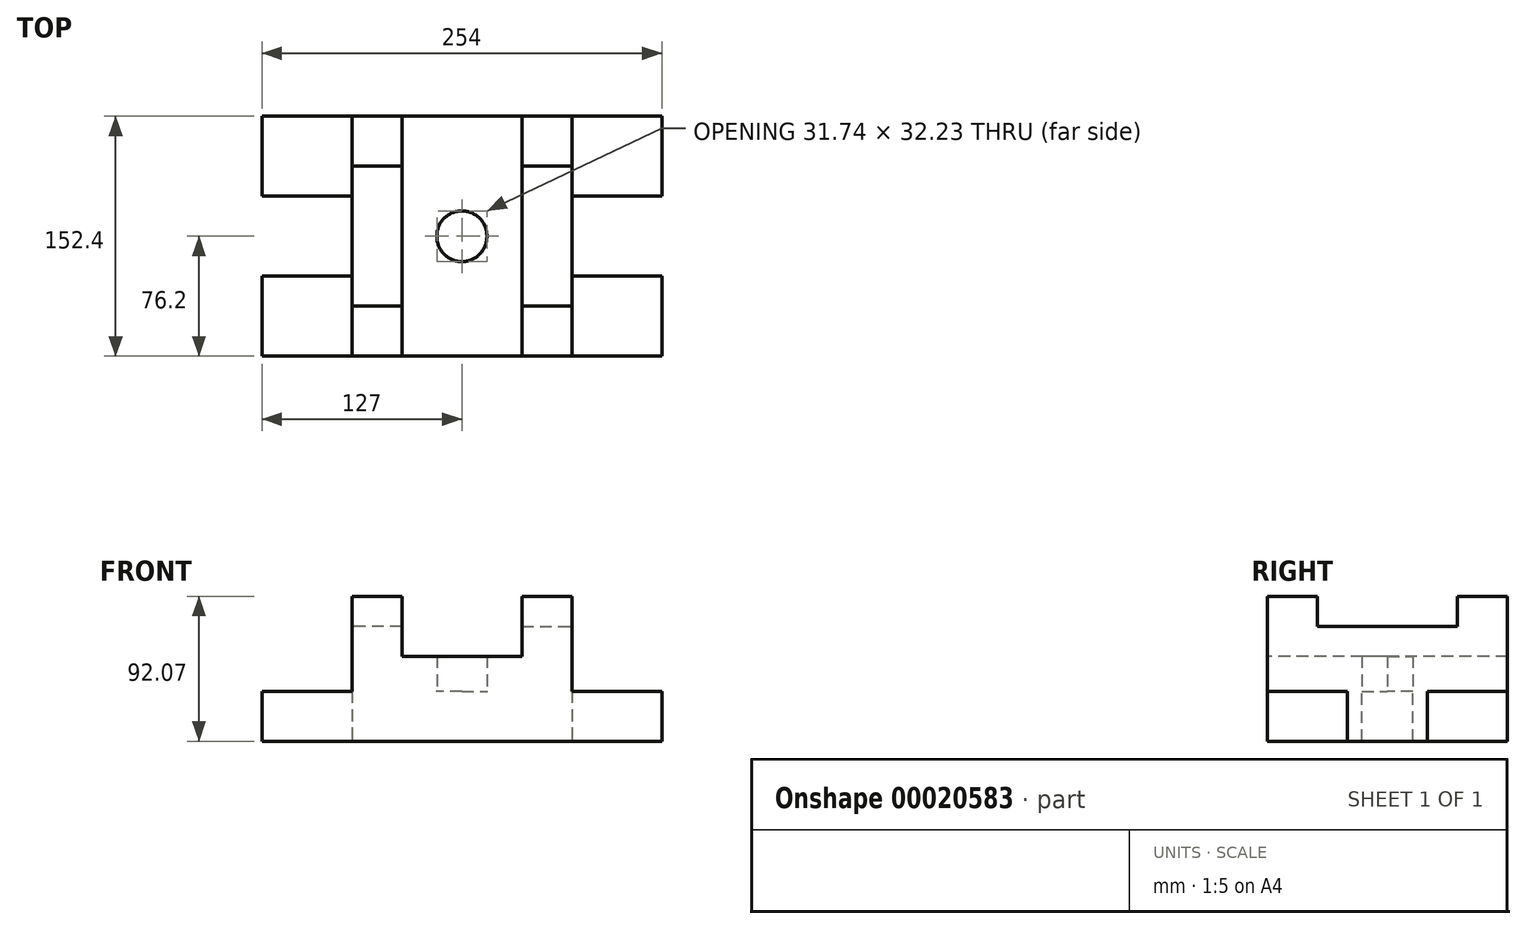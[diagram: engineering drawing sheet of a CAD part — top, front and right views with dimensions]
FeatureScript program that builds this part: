
annotation { "Feature Type Name" : "Feature", "Feature Type Description" : "" }
export const myFeature = defineFeature(function(context is Context, id is Id, definition is map)
    precondition{}
    {
        {
            var Q0;
            Q0=qCreatedBy(makeId("Front.planeOp"),FACE);
            var sketch = newSketch(context, id + "F0", { "sketchPlane" : qUnion([Q0])});
            skLineSegment(sketch, "E0.top", {"start": v(-69.85, -31.75) * mm, "end": v(57.15, -31.75) * mm});
            skLineSegment(sketch, "E0.left", {"start": v(-69.85, 22.22) * mm, "end": v(-69.85, -31.75) * mm});
            skLineSegment(sketch, "E0.right", {"start": v(57.15, 0) * mm, "end": v(57.15, -31.75) * mm});
            skLineSegment(sketch, "E1.bottom", {"start": v(0, 60.33) * mm, "end": v(0, 60.33) * mm});
            skLineSegment(sketch, "E1.top", {"start": v(0, 0) * mm, "end": v(0, 0) * mm});
            skLineSegment(sketch, "E1.left", {"start": v(0, 60.33) * mm, "end": v(0, 0) * mm});
            skLineSegment(sketch, "E1.right", {"start": v(0, 60.33) * mm, "end": v(0, 0) * mm});
            skLineSegment(sketch, "E2.bottom", {"start": v(0, 0) * mm, "end": v(57.15, 0) * mm});
            skLineSegment(sketch, "E2.top", {"start": v(0, 0) * mm, "end": v(57.15, 0) * mm});
            skLineSegment(sketch, "E2.right", {"start": v(57.15, 0) * mm, "end": v(57.15, 0) * mm});
            skLineSegment(sketch, "E3", {"start": v(-69.85, 22.22) * mm, "end": v(-31.75, 22.22) * mm});
            skLineSegment(sketch, "E4", {"start": v(-31.75, 41.27) * mm, "end": v(-31.75, 60.32) * mm});
            skLineSegment(sketch, "E5", {"start": v(-31.75, 60.33) * mm, "end": v(0, 60.33) * mm});
            skLineSegment(sketch, "E6", {"start": v(-31.75, 41.27) * mm, "end": v(0, 41.27) * mm});
            skLineSegment(sketch, "E7", {"start": v(-31.75, 41.27) * mm, "end": v(-31.75, 22.22) * mm});
            skLineSegment(sketch, "E8", {"start": v(0, 0) * mm, "end": v(0, -31.75) * mm});
            skSolve(sketch);
        }
        {
            var Q0;
            Q0=makeQuery(id+"F0.imprint","IMPRINT",FACE,{"disambiguationData":[TD([[makeQuery(id+"F0.imprint","IMPRINT",EDGE,{"derivedFrom":sQuery(id+"F0.wireOp",EDGE,"E0.top")}),1.0]])]});
            extrude(context, id + "F1", {"entities" : qUnion([Q0]), "oppositeDirection" : true, "depth" : 50.8 * mm});
        }
        {
            var Q0;
            Q0=makeQuery(id+"F0.imprint","IMPRINT",FACE,{"disambiguationData":[TD([[makeQuery(id+"F0.imprint","IMPRINT",EDGE,{"derivedFrom":sQuery(id+"F0.wireOp",EDGE,"E4")}),-1.0]])]});
            extrude(context, id + "F2", {"entities" : qUnion([Q0]), "oppositeDirection" : true, "depth" : 31.75 * mm});
        }
        {
            var Q0;
            {var subQ3=sQuery(id+"F0.wireOp",EDGE,"E0.left");Q0=makeQuery(id+"F0.imprint","IMPRINT",FACE,{"disambiguationData":[TD([[makeQuery(id+"F0.imprint","IMPRINT",EDGE,{"derivedFrom":subQ3}),1.0]])]});}
            extrude(context, id + "F3", {"entities" : qUnion([Q0]), "oppositeDirection" : true, "depth" : 76.2 * mm});
        }
        {
            var Q0;
            Q0=qCreatedBy(makeId("Top.planeOp"),FACE);
            var sketch = newSketch(context, id + "F4", { "sketchPlane" : qUnion([Q0])});
            skCircle(sketch, "E9", {"center": v(-69.8, 75.92) * mm, "radius": 15.83 * mm});
            skSolve(sketch);
        }
        {
            var Q0;
            Q0=makeQuery(id+"F4.imprint","IMPRINT",FACE,{"disambiguationData":[TD([[makeQuery(id+"F4.imprint","IMPRINT",EDGE,{"derivedFrom":sQuery(id+"F4.wireOp",EDGE,"E9")}),1.0]])]});
            extrude(context, id + "F5", {"entities" : qUnion([Q0]), "operationType" : NewBodyOperationType.REMOVE, "endBound" : BoundingType.THROUGH_ALL, "depth" : 25.4 * mm});
        }
        {
            var Q0;
            Q0=qCreatedBy(makeId("Top.planeOp"),FACE);
            var sketch = newSketch(context, id + "F6", { "sketchPlane" : qUnion([Q0])});
            skCircle(sketch, "E10", {"center": v(-69.77, 76.23) * mm, "radius": 16.26 * mm});
            skSolve(sketch);
        }
        {
            var Q0;
            Q0=makeQuery(id+"F6.imprint","IMPRINT",FACE,{"disambiguationData":[TD([[makeQuery(id+"F6.imprint","IMPRINT",EDGE,{"derivedFrom":sQuery(id+"F6.wireOp",EDGE,"E10")}),1.0]])]});
            extrude(context, id + "F7", {"entities" : qUnion([Q0]), "operationType" : NewBodyOperationType.REMOVE, "endBound" : BoundingType.THROUGH_ALL, "oppositeDirection" : true, "depth" : 25.4 * mm});
        }
        {
            var Q0;
            Q0=makeQuery(id+"F3.opExtrude","SWEPT_BODY",BODY,{"disambiguationData":[OSD([sQuery(id+"F0.wireOp",EDGE,"E0.top"),sQuery(id+"F0.wireOp",EDGE,"E0.left"),sQuery(id+"F0.wireOp",EDGE,"E1.right"),sQuery(id+"F0.wireOp",EDGE,"E3"),sQuery(id+"F0.wireOp",EDGE,"E6"),sQuery(id+"F0.wireOp",EDGE,"E7"),sQuery(id+"F0.wireOp",EDGE,"E8")])]});
            var Q1;
            Q1=makeQuery(id+"F2.opExtrude","SWEPT_BODY",BODY,{"disambiguationData":[OSD([sQuery(id+"F0.wireOp",EDGE,"E1.right"),sQuery(id+"F0.wireOp",EDGE,"E4"),sQuery(id+"F0.wireOp",EDGE,"E5"),sQuery(id+"F0.wireOp",EDGE,"E6")])]});
            var Q2;
            Q2=makeQuery(id+"F1.opExtrude","SWEPT_BODY",BODY,{"disambiguationData":[OSD([sQuery(id+"F0.wireOp",EDGE,"E0.top"),sQuery(id+"F0.wireOp",EDGE,"E0.right"),sQuery(id+"F0.wireOp",EDGE,"E2.top"),sQuery(id+"F0.wireOp",EDGE,"E8")])]});
            var Q3;
            Q3=makeQuery(id+"F3.opExtrude","CAP_FACE",FACE,{"disambiguationData":[OSD([sQuery(id+"F0.wireOp",EDGE,"E0.top"),sQuery(id+"F0.wireOp",EDGE,"E0.left"),sQuery(id+"F0.wireOp",EDGE,"E1.right"),sQuery(id+"F0.wireOp",EDGE,"E3"),sQuery(id+"F0.wireOp",EDGE,"E6"),sQuery(id+"F0.wireOp",EDGE,"E7"),sQuery(id+"F0.wireOp",EDGE,"E8")])],"isStart":false});
            mirror(context, id + "F8", {"entities" : qUnion([Q0, Q1, Q2]), "mirrorPlane" : qUnion([Q3])});
        }
        {
            var Q0;
            Q0=makeQuery(id+"F1.opExtrude","SWEPT_BODY",BODY,{"disambiguationData":[OSD([sQuery(id+"F0.wireOp",EDGE,"E0.top"),sQuery(id+"F0.wireOp",EDGE,"E0.right"),sQuery(id+"F0.wireOp",EDGE,"E2.top"),sQuery(id+"F0.wireOp",EDGE,"E8")])]});
            var Q1;
            Q1=makeQuery(id+"F2.opExtrude","SWEPT_BODY",BODY,{"disambiguationData":[OSD([sQuery(id+"F0.wireOp",EDGE,"E1.right"),sQuery(id+"F0.wireOp",EDGE,"E4"),sQuery(id+"F0.wireOp",EDGE,"E5"),sQuery(id+"F0.wireOp",EDGE,"E6")])]});
            var Q2;
            Q2=makeQuery(id+"F3.opExtrude","SWEPT_BODY",BODY,{"disambiguationData":[OSD([sQuery(id+"F0.wireOp",EDGE,"E0.top"),sQuery(id+"F0.wireOp",EDGE,"E0.left"),sQuery(id+"F0.wireOp",EDGE,"E1.right"),sQuery(id+"F0.wireOp",EDGE,"E3"),sQuery(id+"F0.wireOp",EDGE,"E6"),sQuery(id+"F0.wireOp",EDGE,"E7"),sQuery(id+"F0.wireOp",EDGE,"E8")])]});
            var Q3;
            Q3=makeQuery(id+"F8.opPattern","COPY",BODY,{"derivedFrom":makeQuery(id+"F2.opExtrude","SWEPT_BODY",BODY,{"disambiguationData":[OSD([sQuery(id+"F0.wireOp",EDGE,"E1.right"),sQuery(id+"F0.wireOp",EDGE,"E4"),sQuery(id+"F0.wireOp",EDGE,"E5"),sQuery(id+"F0.wireOp",EDGE,"E6")])]}),"instanceName":"1"});
            var Q4;
            Q4=makeQuery(id+"F8.opPattern","COPY",BODY,{"derivedFrom":makeQuery(id+"F1.opExtrude","SWEPT_BODY",BODY,{"disambiguationData":[OSD([sQuery(id+"F0.wireOp",EDGE,"E0.top"),sQuery(id+"F0.wireOp",EDGE,"E0.right"),sQuery(id+"F0.wireOp",EDGE,"E2.top"),sQuery(id+"F0.wireOp",EDGE,"E8")])]}),"instanceName":"1"});
            var Q5;
            Q5=makeQuery(id+"F8.opPattern","COPY",BODY,{"derivedFrom":makeQuery(id+"F3.opExtrude","SWEPT_BODY",BODY,{"disambiguationData":[OSD([sQuery(id+"F0.wireOp",EDGE,"E0.top"),sQuery(id+"F0.wireOp",EDGE,"E0.left"),sQuery(id+"F0.wireOp",EDGE,"E1.right"),sQuery(id+"F0.wireOp",EDGE,"E3"),sQuery(id+"F0.wireOp",EDGE,"E6"),sQuery(id+"F0.wireOp",EDGE,"E7"),sQuery(id+"F0.wireOp",EDGE,"E8")])]}),"instanceName":"1"});
            var Q6;
            Q6=makeQuery(id+"F8.opPattern","COPY",FACE,{"derivedFrom":makeQuery(id+"F3.opExtrude","SWEPT_FACE",FACE,{"disambiguationData":[OSD([sQuery(id+"F0.wireOp",EDGE,"E0.left")])]}),"instanceName":"1"});
            mirror(context, id + "F9", {"operationType" : NewBodyOperationType.ADD, "entities" : qUnion([Q0, Q1, Q2, Q3, Q4, Q5]), "mirrorPlane" : qUnion([Q6])});
        }
    });
